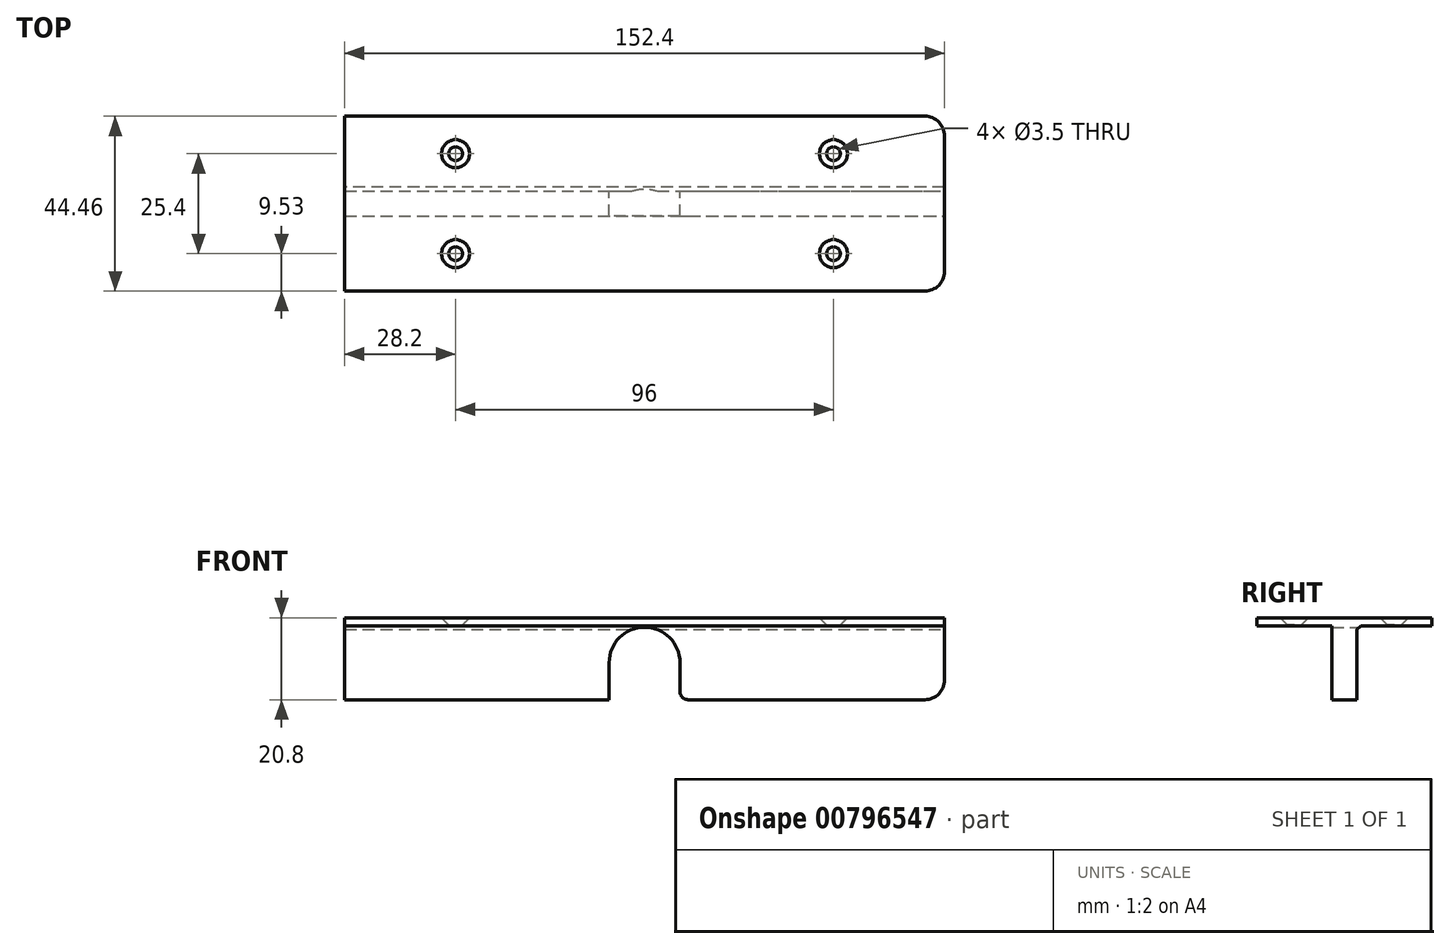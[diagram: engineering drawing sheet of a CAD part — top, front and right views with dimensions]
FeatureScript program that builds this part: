
annotation { "Feature Type Name" : "Feature", "Feature Type Description" : "" }
export const myFeature = defineFeature(function(context is Context, id is Id, definition is map)
    precondition{}
    {
        {
            var Q0;
            Q0=qCreatedBy(makeId("Top.planeOp"),FACE);
            var sketch = newSketch(context, id + "F0", { "sketchPlane" : qUnion([Q0])});
            skLineSegment(sketch, "E0.bottom", {"start": v(76.2, -22.23) * mm, "end": v(-76.2, -22.23) * mm});
            skLineSegment(sketch, "E0.top", {"start": v(76.2, 22.22) * mm, "end": v(-76.2, 22.22) * mm});
            skLineSegment(sketch, "E0.left", {"start": v(76.2, -22.23) * mm, "end": v(76.2, 22.22) * mm});
            skLineSegment(sketch, "E0.right", {"start": v(-76.2, -22.23) * mm, "end": v(-76.2, 22.22) * mm});
            skPoint(sketch, "E0.middle", {"position": v(0, 0) * mm});
            skSolve(sketch);
        }
        {
            var Q0;
            Q0=qSketchRegion(id+"F0",true);
            extrude(context, id + "F1", {"entities" : qUnion([Q0]), "depth" : 2 * mm, "offsetDistance" : 25 * mm});
        }
        {
            var Q0;
            Q0=makeQuery(id+"F1.opExtrude","CAP_FACE",FACE,{"disambiguationData":[OSD([sQuery(id+"F0.wireOp",EDGE,"E0.bottom"),sQuery(id+"F0.wireOp",EDGE,"E0.top"),sQuery(id+"F0.wireOp",EDGE,"E0.left"),sQuery(id+"F0.wireOp",EDGE,"E0.right")])],"isStart":true});
            var sketch = newSketch(context, id + "F2", { "sketchPlane" : qUnion([Q0])});
            skLineSegment(sketch, "E1.bottom", {"start": v(-76.2, -3.18) * mm, "end": v(76.2, -3.18) * mm});
            skLineSegment(sketch, "E1.top", {"start": v(-76.2, 3.17) * mm, "end": v(76.2, 3.17) * mm});
            skLineSegment(sketch, "E1.left", {"start": v(-76.2, -3.18) * mm, "end": v(-76.2, 3.18) * mm});
            skLineSegment(sketch, "E1.right", {"start": v(76.2, -3.18) * mm, "end": v(76.2, 3.18) * mm});
            skPoint(sketch, "E1.middle", {"position": v(0, 0) * mm});
            skSolve(sketch);
        }
        {
            var Q0;
            Q0=makeQuery(id+"F2.imprint","IMPRINT",FACE,{"disambiguationData":[TD([[makeQuery(id+"F2.imprint","IMPRINT",EDGE,{"derivedFrom":sQuery(id+"F2.wireOp",EDGE,"E1.bottom")}),1.0]])]});
            extrude(context, id + "F3", {"entities" : qUnion([Q0]), "operationType" : NewBodyOperationType.ADD, "depth" : 18.8 * mm, "offsetDistance" : 25 * mm});
        }
        {
            var Q0;
            {var subQ0=sQuery(id+"F0.wireOp",EDGE,"E0.right");var subQ1=sQuery(id+"F0.wireOp",EDGE,"E0.left");var subQ2=sQuery(id+"F0.wireOp",EDGE,"E0.top");Q0=makeQuery(id+"F3.boolean.opBoolean","SPLIT",FACE,{"disambiguationData":[TD([makeQuery(id+"F1.opExtrude","SWEPT_FACE",FACE,{"disambiguationData":[OSD([subQ2])]})])],"derivedFrom":makeQuery(id+"F1.opExtrude","CAP_FACE",FACE,{"disambiguationData":[OSD([sQuery(id+"F0.wireOp",EDGE,"E0.bottom"),subQ2,subQ1,subQ0])],"isStart":true})});}
            var sketch = newSketch(context, id + "F4", { "sketchPlane" : qUnion([Q0])});
            skLineSegment(sketch, "E2", {"start": v(76.2, -12.7) * mm, "end": v(-76.2, -12.7) * mm, "construction": true});
            skCircle(sketch, "E3", {"center": v(48, -12.7) * mm, "radius": 1.75 * mm});
            skCircle(sketch, "E4.0.1.0", {"center": v(48, 12.7) * mm, "radius": 1.75 * mm});
            skCircle(sketch, "E4.1.0.0", {"center": v(-48, -12.7) * mm, "radius": 1.75 * mm});
            skCircle(sketch, "E4.1.1.0", {"center": v(-48, 12.7) * mm, "radius": 1.75 * mm});
            skLineSegment(sketch, "E4.direction1", {"start": v(48, -12.7) * mm, "end": v(-48, -12.7) * mm, "construction": true});
            skLineSegment(sketch, "E4.direction2", {"start": v(48, -12.7) * mm, "end": v(48, 12.7) * mm, "construction": true});
            skSolve(sketch);
        }
        {
            var Q0;
            Q0=makeQuery(id+"F4.imprint","IMPRINT",FACE,{"disambiguationData":[TD([[makeQuery(id+"F4.imprint","IMPRINT",EDGE,{"derivedFrom":sQuery(id+"F4.wireOp",EDGE,"E3")}),1.0]])]});
            var Q1;
            Q1=makeQuery(id+"F4.imprint","IMPRINT",FACE,{"disambiguationData":[TD([[makeQuery(id+"F4.imprint","IMPRINT",EDGE,{"derivedFrom":sQuery(id+"F4.wireOp",EDGE,"E4.1.0.0")}),1.0]])]});
            var Q2;
            Q2=makeQuery(id+"F4.imprint","IMPRINT",FACE,{"disambiguationData":[TD([[makeQuery(id+"F4.imprint","IMPRINT",EDGE,{"derivedFrom":sQuery(id+"F4.wireOp",EDGE,"E4.2.0.0")}),1.0]])]});
            var Q3;
            Q3=makeQuery(id+"F4.imprint","IMPRINT",FACE,{"disambiguationData":[TD([[makeQuery(id+"F4.imprint","IMPRINT",EDGE,{"derivedFrom":sQuery(id+"F4.wireOp",EDGE,"E4.3.0.0")}),1.0]])]});
            var Q4;
            Q4=makeQuery(id+"F4.imprint","IMPRINT",FACE,{"disambiguationData":[TD([[makeQuery(id+"F4.imprint","IMPRINT",EDGE,{"derivedFrom":sQuery(id+"F4.wireOp",EDGE,"E4.3.1.0")}),1.0]])]});
            var Q5;
            Q5=makeQuery(id+"F4.imprint","IMPRINT",FACE,{"disambiguationData":[TD([[makeQuery(id+"F4.imprint","IMPRINT",EDGE,{"derivedFrom":sQuery(id+"F4.wireOp",EDGE,"E4.2.1.0")}),1.0]])]});
            var Q6;
            Q6=makeQuery(id+"F4.imprint","IMPRINT",FACE,{"disambiguationData":[TD([[makeQuery(id+"F4.imprint","IMPRINT",EDGE,{"derivedFrom":sQuery(id+"F4.wireOp",EDGE,"E4.1.1.0")}),1.0]])]});
            var Q7;
            Q7=makeQuery(id+"F4.imprint","IMPRINT",FACE,{"disambiguationData":[TD([[makeQuery(id+"F4.imprint","IMPRINT",EDGE,{"derivedFrom":sQuery(id+"F4.wireOp",EDGE,"E4.0.1.0")}),1.0]])]});
            extrude(context, id + "F5", {"entities" : qUnion([Q0, Q1, Q2, Q3, Q4, Q5, Q6, Q7]), "operationType" : NewBodyOperationType.REMOVE, "oppositeDirection" : true, "depth" : 25 * mm, "offsetDistance" : 25 * mm});
        }
        {
            var Q0;
            Q0=makeQuery(id+"F3.opExtrude","SWEPT_FACE",FACE,{"disambiguationData":[OSD([sQuery(id+"F2.wireOp",EDGE,"E1.bottom")])]});
            var sketch = newSketch(context, id + "F6", { "sketchPlane" : qUnion([Q0])});
            skLineSegment(sketch, "E5", {"start": v(-76.2, -9.4) * mm, "end": v(76.2, -9.4) * mm, "construction": true});
            skCircle(sketch, "E6", {"center": v(0, -9.4) * mm, "radius": 9 * mm});
            skCircle(sketch, "E7", {"center": v(0, -9.4) * mm, "radius": 4.76 * mm, "construction": true});
            skPoint(sketch, "E8", {"position": v(9, -9.4) * mm});
            skPoint(sketch, "E9", {"position": v(-9, -9.4) * mm});
            skLineSegment(sketch, "E10", {"start": v(-9, -9.4) * mm, "end": v(-9, -18.8) * mm});
            skLineSegment(sketch, "E11", {"start": v(9, -9.4) * mm, "end": v(9, -18.8) * mm});
            skLineSegment(sketch, "E12", {"start": v(9, -18.8) * mm, "end": v(-9, -18.8) * mm});
            skSolve(sketch);
        }
        {
            var Q0;
            Q0=makeQuery(id+"F6.imprint","IMPRINT",FACE,{"disambiguationData":[TD([[makeQuery(id+"F6.imprint","IMPRINT",EDGE,{"derivedFrom":sQuery(id+"F6.wireOp",EDGE,"E6")}),1.0]])]});
            var Q1;
            {var subQ0=sQuery(id+"F6.wireOp",EDGE,"E10");Q1=makeQuery(id+"F6.imprint","IMPRINT",FACE,{"disambiguationData":[TD([[makeQuery(id+"F6.imprint","IMPRINT",EDGE,{"derivedFrom":subQ0}),1.0]])]});}
            var Q2;
            Q2=sQuery(id+"F6.wireOp",EDGE,"E6");
            extrude(context, id + "F7", {"entities" : qUnion([Q0, Q1]), "operationType" : NewBodyOperationType.REMOVE, "surfaceEntities" : qUnion([Q2]), "endBound" : BoundingType.THROUGH_ALL, "oppositeDirection" : true, "depth" : 25 * mm, "offsetDistance" : 25 * mm});
        }
        {
            var Q0;
            Q0=makeQuery(id+"F5.boolean.opBoolean","INTERSECT",EDGE,{"derivedFrom":[makeQuery(id+"F1.opExtrude","CAP_FACE",FACE,{"disambiguationData":[OSD([sQuery(id+"F0.wireOp",EDGE,"E0.bottom"),sQuery(id+"F0.wireOp",EDGE,"E0.top"),sQuery(id+"F0.wireOp",EDGE,"E0.left"),sQuery(id+"F0.wireOp",EDGE,"E0.right")])],"isStart":false}),makeQuery(id+"F5.opExtrude","SWEPT_FACE",FACE,{"disambiguationData":[OSD([sQuery(id+"F4.wireOp",EDGE,"E4.0.1.0")])]})]});
            var Q1;
            Q1=makeQuery(id+"F5.boolean.opBoolean","INTERSECT",EDGE,{"derivedFrom":[makeQuery(id+"F1.opExtrude","CAP_FACE",FACE,{"disambiguationData":[OSD([sQuery(id+"F0.wireOp",EDGE,"E0.bottom"),sQuery(id+"F0.wireOp",EDGE,"E0.top"),sQuery(id+"F0.wireOp",EDGE,"E0.left"),sQuery(id+"F0.wireOp",EDGE,"E0.right")])],"isStart":false}),makeQuery(id+"F5.opExtrude","SWEPT_FACE",FACE,{"disambiguationData":[OSD([sQuery(id+"F4.wireOp",EDGE,"E4.1.1.0")])]})]});
            var Q2;
            Q2=makeQuery(id+"F5.boolean.opBoolean","INTERSECT",EDGE,{"derivedFrom":[makeQuery(id+"F1.opExtrude","CAP_FACE",FACE,{"disambiguationData":[OSD([sQuery(id+"F0.wireOp",EDGE,"E0.bottom"),sQuery(id+"F0.wireOp",EDGE,"E0.top"),sQuery(id+"F0.wireOp",EDGE,"E0.left"),sQuery(id+"F0.wireOp",EDGE,"E0.right")])],"isStart":false}),makeQuery(id+"F5.opExtrude","SWEPT_FACE",FACE,{"disambiguationData":[OSD([sQuery(id+"F4.wireOp",EDGE,"E4.2.1.0")])]})]});
            var Q3;
            Q3=makeQuery(id+"F5.boolean.opBoolean","INTERSECT",EDGE,{"derivedFrom":[makeQuery(id+"F1.opExtrude","CAP_FACE",FACE,{"disambiguationData":[OSD([sQuery(id+"F0.wireOp",EDGE,"E0.bottom"),sQuery(id+"F0.wireOp",EDGE,"E0.top"),sQuery(id+"F0.wireOp",EDGE,"E0.left"),sQuery(id+"F0.wireOp",EDGE,"E0.right")])],"isStart":false}),makeQuery(id+"F5.opExtrude","SWEPT_FACE",FACE,{"disambiguationData":[OSD([sQuery(id+"F4.wireOp",EDGE,"E4.3.1.0")])]})]});
            var Q4;
            Q4=makeQuery(id+"F5.boolean.opBoolean","INTERSECT",EDGE,{"derivedFrom":[makeQuery(id+"F1.opExtrude","CAP_FACE",FACE,{"disambiguationData":[OSD([sQuery(id+"F0.wireOp",EDGE,"E0.bottom"),sQuery(id+"F0.wireOp",EDGE,"E0.top"),sQuery(id+"F0.wireOp",EDGE,"E0.left"),sQuery(id+"F0.wireOp",EDGE,"E0.right")])],"isStart":false}),makeQuery(id+"F5.opExtrude","SWEPT_FACE",FACE,{"disambiguationData":[OSD([sQuery(id+"F4.wireOp",EDGE,"E4.3.0.0")])]})]});
            var Q5;
            Q5=makeQuery(id+"F5.boolean.opBoolean","INTERSECT",EDGE,{"derivedFrom":[makeQuery(id+"F1.opExtrude","CAP_FACE",FACE,{"disambiguationData":[OSD([sQuery(id+"F0.wireOp",EDGE,"E0.bottom"),sQuery(id+"F0.wireOp",EDGE,"E0.top"),sQuery(id+"F0.wireOp",EDGE,"E0.left"),sQuery(id+"F0.wireOp",EDGE,"E0.right")])],"isStart":false}),makeQuery(id+"F5.opExtrude","SWEPT_FACE",FACE,{"disambiguationData":[OSD([sQuery(id+"F4.wireOp",EDGE,"E4.2.0.0")])]})]});
            var Q6;
            Q6=makeQuery(id+"F5.boolean.opBoolean","INTERSECT",EDGE,{"derivedFrom":[makeQuery(id+"F1.opExtrude","CAP_FACE",FACE,{"disambiguationData":[OSD([sQuery(id+"F0.wireOp",EDGE,"E0.bottom"),sQuery(id+"F0.wireOp",EDGE,"E0.top"),sQuery(id+"F0.wireOp",EDGE,"E0.left"),sQuery(id+"F0.wireOp",EDGE,"E0.right")])],"isStart":false}),makeQuery(id+"F5.opExtrude","SWEPT_FACE",FACE,{"disambiguationData":[OSD([sQuery(id+"F4.wireOp",EDGE,"E4.1.0.0")])]})]});
            var Q7;
            Q7=makeQuery(id+"F5.boolean.opBoolean","INTERSECT",EDGE,{"derivedFrom":[makeQuery(id+"F1.opExtrude","CAP_FACE",FACE,{"disambiguationData":[OSD([sQuery(id+"F0.wireOp",EDGE,"E0.bottom"),sQuery(id+"F0.wireOp",EDGE,"E0.top"),sQuery(id+"F0.wireOp",EDGE,"E0.left"),sQuery(id+"F0.wireOp",EDGE,"E0.right")])],"isStart":false}),makeQuery(id+"F5.opExtrude","SWEPT_FACE",FACE,{"disambiguationData":[OSD([sQuery(id+"F4.wireOp",EDGE,"E3")])]})]});
            chamfer(context, id + "F8", {"entities" : qUnion([Q0, Q1, Q2, Q3, Q4, Q5, Q6, Q7]), "width" : 1.8 * mm, "tangentPropagation" : true});
        }
        {
            var Q0;
            Q0=makeQuery(id+"F3.opExtrude","CAP_EDGE",EDGE,{"disambiguationData":[OSD([sQuery(id+"F2.wireOp",EDGE,"E1.bottom")])],"isStart":true});
            var Q1;
            Q1=makeQuery(id+"F3.opExtrude","CAP_EDGE",EDGE,{"disambiguationData":[OSD([sQuery(id+"F2.wireOp",EDGE,"E1.top")])],"isStart":true});
            chamfer(context, id + "F9", {"entities" : qUnion([Q0, Q1]), "width" : 1 * mm, "tangentPropagation" : true});
        }
        {
            var Q0;
            Q0=makeQuery(id+"F7.boolean.opBoolean","COPY",EDGE,{"derivedFrom":makeQuery(id+"F7.opExtrude","SWEPT_EDGE",EDGE,{"disambiguationData":[OSD([sQuery(id+"F2.wireOp",EDGE,"E1.bottom"),sQuery(id+"F6.wireOp",EDGE,"E10"),sQuery(id+"F6.wireOp",EDGE,"E12")])]})});
            var Q1;
            Q1=makeQuery(id+"F7.boolean.opBoolean","COPY",EDGE,{"derivedFrom":makeQuery(id+"F7.opExtrude","SWEPT_EDGE",EDGE,{"disambiguationData":[OSD([sQuery(id+"F2.wireOp",EDGE,"E1.bottom"),sQuery(id+"F6.wireOp",EDGE,"E11"),sQuery(id+"F6.wireOp",EDGE,"E12")])]})});
            fillet(context, id + "F10", {"entities" : qUnion([Q0, Q1]), "radius" : 2 * mm, "tangentPropagation" : true, "allowEdgeOverflow" : false});
        }
        {
            var Q0;
            Q0=makeQuery(id+"F3.opExtrude","CAP_EDGE",EDGE,{"disambiguationData":[OSD([sQuery(id+"F2.wireOp",EDGE,"E1.right")])],"isStart":false});
            var Q1;
            Q1=makeQuery(id+"F1.opExtrude","SWEPT_EDGE",EDGE,{"disambiguationData":[OSD([sQuery(id+"F0.wireOp",EDGE,"E0.bottom"),sQuery(id+"F0.wireOp",EDGE,"E0.left")])]});
            var Q2;
            Q2=makeQuery(id+"F1.opExtrude","SWEPT_EDGE",EDGE,{"disambiguationData":[OSD([sQuery(id+"F0.wireOp",EDGE,"E0.top"),sQuery(id+"F0.wireOp",EDGE,"E0.left")])]});
            fillet(context, id + "F11", {"entities" : qUnion([Q0, Q1, Q2]), "radius" : 5 * mm, "tangentPropagation" : true, "allowEdgeOverflow" : false});
        }
    });
